# Revit family: 0045518 Sylvania Lighting Fixture OPTIX LINEAR SURFACE 1200 3000K ALU DA
name_source: partatom
category: Lighting Fixtures
revit_build: Autodesk Revit 2017 (Build: 20190507_1515(x64)
units: mm (PartAtom-declared; Revit-internal decimal feet)

## family parameters
Cut with Voids When Loaded = No
Host = Face
Light Source = Yes
OmniClass Number = 23.80.70.00
OmniClass Title = Lighting
Part Type = Normal
Room Calculation Point = No
Round Connector Dimension = Use Diameter
Shared = No

## types (1)
- 0045518 OPTIX LIN S 1200 3K ALU DA
    Apparent Load = 27 VA
    Assembly Code = D5020200
    AssetType = Fixed
    ClassificationName = Uniclass2015
    ClassificationValue = EF_70_80
    Color Filter = 16777215
    Cost = 0 $
    Default Elevation = 1219 mm
    Description = OPTIX LINEAR SURFACE 1200 3000K ALU DA is a high efficacy low glare linear luminaire for office and education applications. Suitable for continuous  light line installations with accessories separately available. Surface and suspended mounting. Size: 1129x90x80mm. Aluminised plastic extra low glare optics in a single line configuration. White RAL9016 fixture body. DALI dimmable. 3000K Warm White LED, CRI>80, chromaticity tolerance of 3-step MacAdam ellipse. Luminous flux 3200lm. Power consumption 27W. Luminaire efficacy 119lm/W. Lumen maintenance of L90B50 > 72000h, L90B10 = 43000h. UGR<19, Luminance at 65°<200 Cd/m2, IK07, IP20. Ultra Low Flicker: <5% Photobiological safety risk group 1. Electrical protection Class I. Glow wire test 850°C.
    Dimming Lamp Color Temperature Shift = <None>
    DocumentationLiterature = http://www.sylvania-lighting.com
    Emit Shape Visible in Rendering = No
    Emit from Circle Diameter = 610 mm
    Height = 86 mm
    IfcExportAs = 119
    IfcExportType = IfcLightFixtureType
    ImpactProtectionIndex = Class I
    InputNominalFrequency = IK07
    InputVoltage = IP20
    Keynote = 0
    LampMacAdamStep = 16500
    LampNominalLuminous = LED
    Length = 1130 mm
    LightOutputRatio = 3
    LuminaireType = 3200 lm
    Manufacturer = Feilo Sylvania
    ManufacturerName = Feilo Sylvania
    Material_1_SYL = <By Category>
    Material_2_SYL = <By Category>
    Material_3_SYL = <By Category>
    Material_4_SYL = <By Category>
    Model = OPTIX LINEAR SURFACE 1200 3000K ALU DA
    ModelNumber = 0045518
    ModelReference = OPTIX LINEAR SURFACE 1200 3000K ALU DA
    Name = OPTIX LINEAR SURFACE 1200 3000K ALU DA
    NominalDepth = 0 mm  [stored 0 ft]
    NominalHeight = 0 mm  [stored 0 ft]
    NominalLength = 0 mm  [stored 0 ft]
    Photometric Web File = 0045518.ies
    PowerConsumption = 1129
    PowerFactor = 0
    Tilt Angle = -90.00°
    Type Image = <None>
    TypeName = OPTIX LINEAR SURFACE 1200 3000K ALU DA
    URL = http://www.sylvania-lighting.com
    Voltage = 0 V
    WarrantyDescription = 0.98
    WarrantyDurationUnit = http://www.sylvania-lighting.com
    Width = 90 mm

note: [stored X ft] marks values corroborated as IEEE doubles in the binary element streams (Revit-internal decimal feet)

## geometry (parser evidence)
native form markers: Sweep x3
no freeform markers — native parametric forms only
